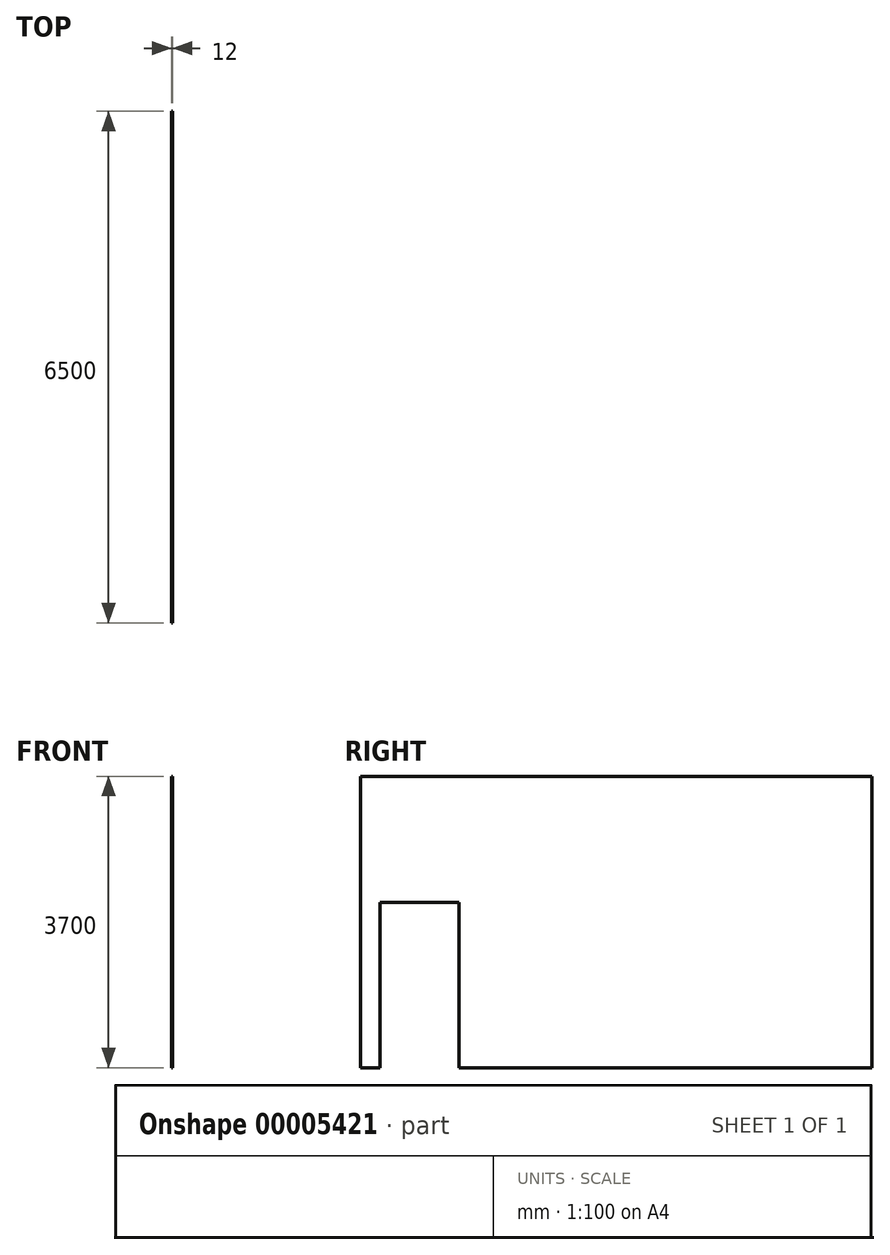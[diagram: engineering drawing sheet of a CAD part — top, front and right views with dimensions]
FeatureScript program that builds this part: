
annotation { "Feature Type Name" : "Feature", "Feature Type Description" : "" }
export const myFeature = defineFeature(function(context is Context, id is Id, definition is map)
    precondition{}
    {
        {
            var Q0;
            Q0=qCreatedBy(makeId("Right.planeOp"),FACE);
            var sketch = newSketch(context, id + "F0", { "sketchPlane" : qUnion([Q0])});
            skLineSegment(sketch, "E0.bottom", {"start": v(-3257.26, 1971.58) * mm, "end": v(3242.74, 1971.58) * mm});
            skLineSegment(sketch, "E0.top", {"start": v(-3257.26, -1728.42) * mm, "end": v(3242.74, -1728.42) * mm});
            skLineSegment(sketch, "E0.left", {"start": v(-3257.26, 1971.58) * mm, "end": v(-3257.26, -1728.42) * mm});
            skLineSegment(sketch, "E0.right", {"start": v(3242.74, 1971.58) * mm, "end": v(3242.74, -1728.42) * mm});
            skSolve(sketch);
        }
        {
            var Q0;
            Q0=makeQuery(id+"F0.imprint","IMPRINT",FACE,{"disambiguationData":[TD([[makeQuery(id+"F0.imprint","IMPRINT",EDGE,{"derivedFrom":sQuery(id+"F0.wireOp",EDGE,"E0.bottom")}),-1.0]])]});
            extrude(context, id + "F1", {"entities" : qUnion([Q0]), "depth" : 12 * mm});
        }
        {
            var Q0;
            Q0=makeQuery(id+"F1.opExtrude","CAP_FACE",FACE,{"disambiguationData":[OSD([sQuery(id+"F0.wireOp",EDGE,"E0.bottom"),sQuery(id+"F0.wireOp",EDGE,"E0.top"),sQuery(id+"F0.wireOp",EDGE,"E0.left"),sQuery(id+"F0.wireOp",EDGE,"E0.right")])],"isStart":false});
            var sketch = newSketch(context, id + "F2", { "sketchPlane" : qUnion([Q0])});
            skLineSegment(sketch, "E1.bottom", {"start": v(-3007.26, -1728.42) * mm, "end": v(-2007.26, -1728.42) * mm});
            skLineSegment(sketch, "E1.top", {"start": v(-3007.26, 371.58) * mm, "end": v(-2007.26, 371.58) * mm});
            skLineSegment(sketch, "E1.left", {"start": v(-3007.26, -1728.42) * mm, "end": v(-3007.26, 371.58) * mm});
            skLineSegment(sketch, "E1.right", {"start": v(-2007.26, -1728.42) * mm, "end": v(-2007.26, 371.58) * mm});
            skSolve(sketch);
        }
        {
            var Q0;
            Q0 = qSketchRegion(id + "F2", true);
            extrude(context, id + "F3", {"entities" : qUnion([Q0]), "operationType" : NewBodyOperationType.REMOVE, "endBound" : BoundingType.THROUGH_ALL, "oppositeDirection" : true, "depth" : 25 * mm});
        }
    });
